# Revit family: Mixer-Basin-Caroma Liano Nexus
name_source: partatom
category: Plumbing Fixtures
revit_build: Autodesk Revit 2013 (Build: 20121003_2115(x64)
units: mm (PartAtom-declared; Revit-internal decimal feet)

## types (1)
- Standard
    Assembly Code = D2020300
    CW Connection = Yes
    CWFU = 1.19
    Connector Radius = 10 mm  [stored 0.0328084 ft]
    Cost = 0 $
    Default Elevation = 0 mm  [stored 0 ft]
    Description = WELS 6 Star rated, 4.5L/min
    HW Connection = Yes
    HWFU = 1.19
    Manufacturer = GWA Bathrooms & Kitchens
    Material_ANZRS = Metal-Steel-Powdercoated-Matte Black
    Model = 96193B6A
    ModifiedIssue_ANZRS = 2013.1 $
    Type Comments = Caroma Liano Nexus Basin Mixer
    URL = http://www.caroma.com.au
    Vent Connection = No
    WELSRating_ANZRS = WELS 6 Star rated, 4.5L/min
    Waste Connection = No

note: [stored X ft] marks values corroborated as IEEE doubles in the binary element streams (Revit-internal decimal feet)

## geometry (parser evidence)
native form markers: Blend x8, Sweep x1
no freeform markers — native parametric forms only
